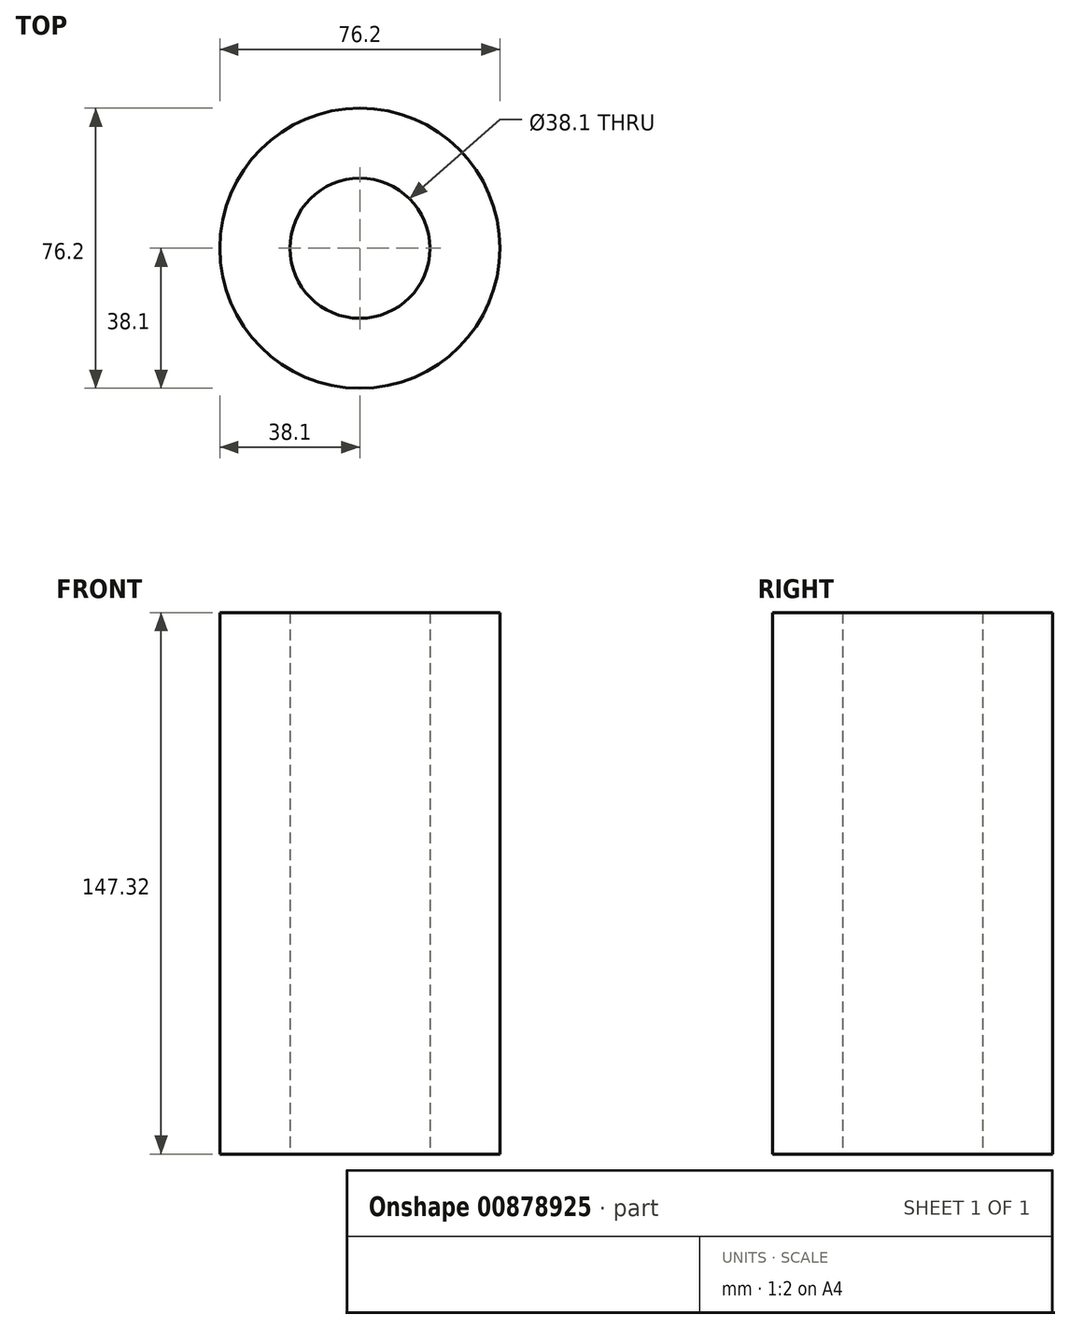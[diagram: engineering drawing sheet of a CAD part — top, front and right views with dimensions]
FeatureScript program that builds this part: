
annotation { "Feature Type Name" : "Feature", "Feature Type Description" : "" }
export const myFeature = defineFeature(function(context is Context, id is Id, definition is map)
    precondition{}
    {
        {
            var Q0;
            Q0=qCreatedBy(makeId("Top.planeOp"),FACE);
            var sketch = newSketch(context, id + "F0", { "sketchPlane" : qUnion([Q0])});
            skCircle(sketch, "E0", {"center": v(0, 0) * mm, "radius": 38.1 * mm});
            skCircle(sketch, "E1", {"center": v(0, 0) * mm, "radius": 19.05 * mm});
            skSolve(sketch);
        }
        {
            var Q0;
            Q0 = qSketchRegion(id + "F0", true);
            extrude(context, id + "F1", {"entities" : qUnion([Q0]), "depth" : 147.32 * mm, "offsetDistance" : 25.4 * mm});
        }
    });
